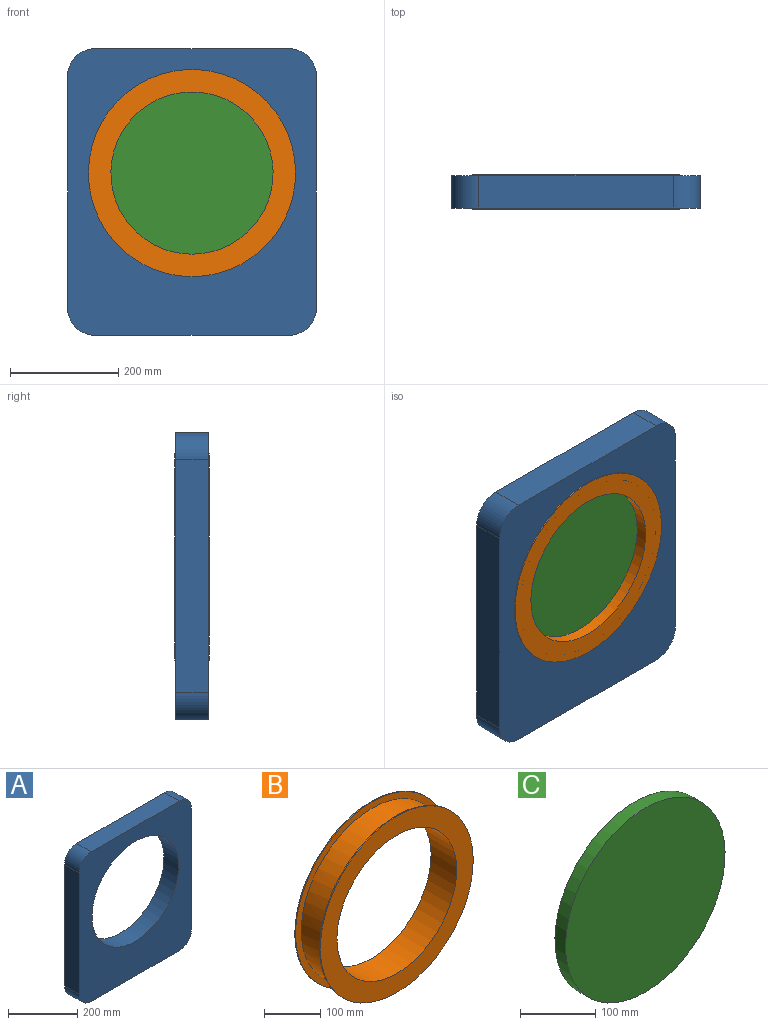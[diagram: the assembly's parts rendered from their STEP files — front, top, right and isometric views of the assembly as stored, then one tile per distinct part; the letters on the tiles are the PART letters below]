
ASSEMBLY  parts=3 mates=2
PART A: 11 faces, bbox 460x60x530 mm
  f0: plane 360x60mm, normal (0,0,1), area 21600mm2, adj f1,f8,f9,f10
  f1: cylinder r=50mm len=60mm, axis (0,1,0), area 4712.4mm2, adj f0,f2,f9,f10
  f2: plane 430x60mm, normal (-1,0,0), area 25800mm2, adj f1,f3,f9,f10
  f3: cylinder r=50mm len=60mm, axis (0,1,0), area 4712.4mm2, adj f2,f4,f9,f10
  f4: plane 360x60mm, normal (0,0,-1), area 21600mm2, adj f3,f5,f9,f10
  f5: cylinder r=50mm len=60mm, axis (0,1,0), area 4712.4mm2, adj f4,f6,f9,f10
  f6: plane 430x60mm, normal (1,0,0), area 25800mm2, adj f5,f8,f9,f10
  f7: cylinder r=177.5mm len=355mm, axis (0,1,0), area 66915.9mm2, adj f9,f10
  f8: cylinder r=50mm len=60mm, axis (0,1,0), area 4712.4mm2, adj f0,f6,f9,f10
  f9: plane 530x460mm, normal (0,-1,0), area 142674.2mm2, adj f0,f1,f2,f3,f4,f5,f6,f7
  f10: plane 530x460mm, normal (0,1,0), area 142674.2mm2, adj f0,f1,f2,f3,f4,f5,f6,f7
PART B: 8 faces, bbox 383x64x383 mm
  f0: cylinder r=177.5mm len=355mm, axis (0,1,0), area 66915.9mm2, adj f5,f7
  f1: cylinder r=150mm len=300mm, axis (0,1,0), area 60318.6mm2, adj f2,f3
  f2: plane 383x383mm, normal (0,-1,0), area 44523.4mm2, adj f1,f4
  f3: plane 383x383mm, normal (0,1,0), area 44523.4mm2, adj f1,f6
  f4: cylinder r=191.5mm len=383mm, axis (0,-1,0), area 2406.5mm2, adj f2,f5
  f5: plane 383x383mm, normal (0,1,0), area 16229.5mm2, adj f0,f4
  f6: cylinder r=191.5mm len=383mm, axis (0,1,0), area 2406.5mm2, adj f3,f7
  f7: plane 383x383mm, normal (0,-1,0), area 16229.5mm2, adj f0,f6
PART C: 3 faces, bbox 300x20x300 mm
  f0: cylinder r=150mm len=300mm, axis (0,1,0), area 18849.6mm2, adj f1,f2
  f1: plane 300x300mm, normal (0,-1,0), area 70685.8mm2, adj f0
  f2: plane 300x300mm, normal (0,1,0), area 70685.8mm2, adj f0
PLACE A t=(0,30,-35)mm
PLACE B at identity
PLACE C at identity fixed
MATE fastened B.f1 <-> C.f0  axis (0,-1,0) through (0,-32,0)mm
MATE fastened A.f7 <-> B.f0  axis (0,-1,0) through (0,-30,0)mm
